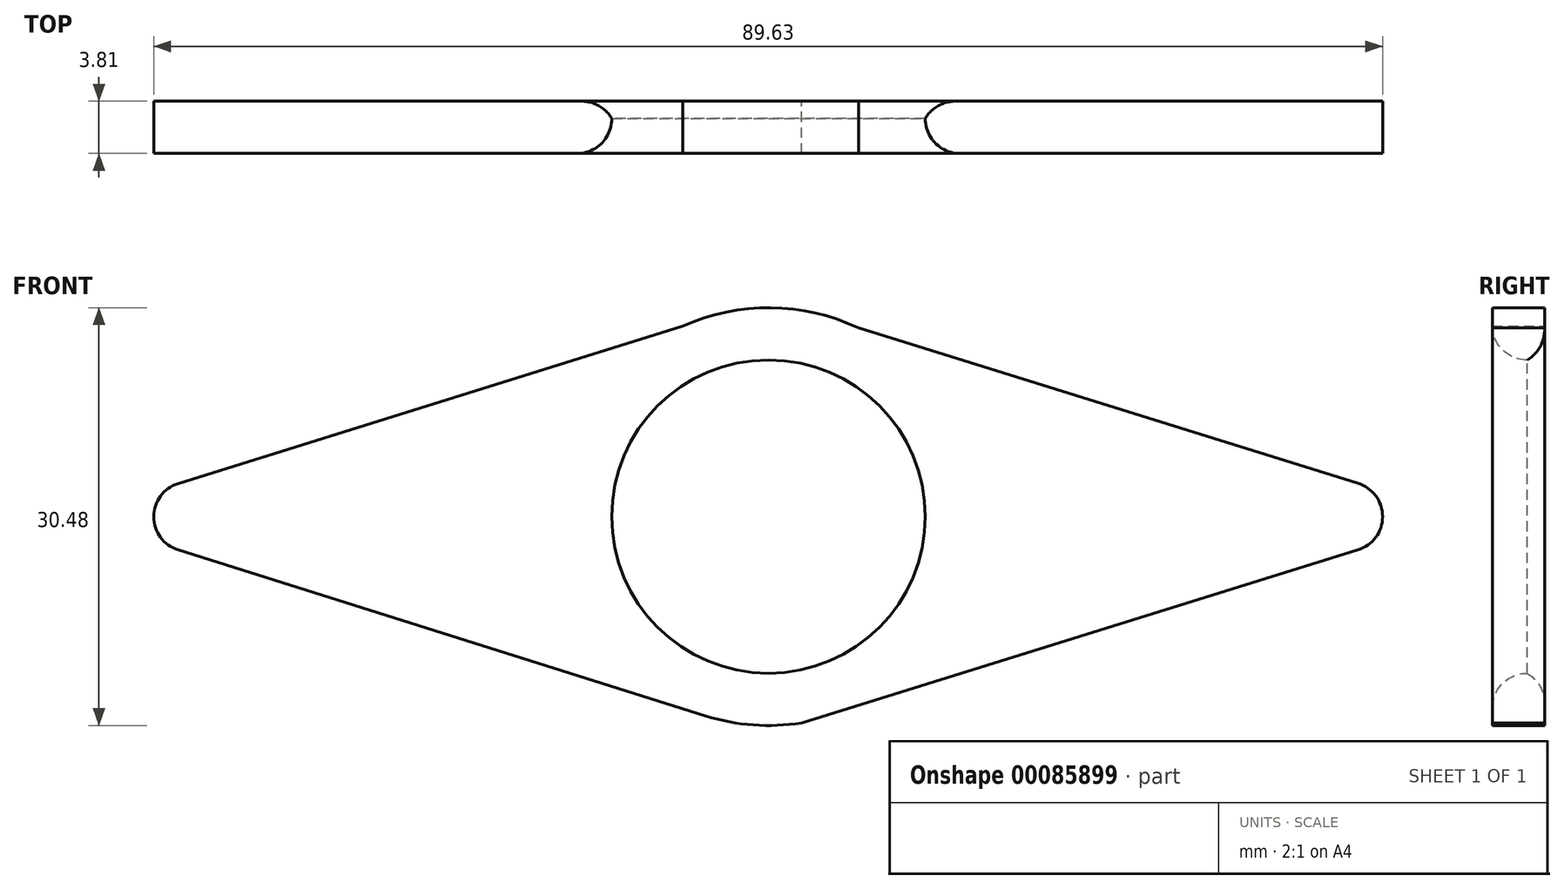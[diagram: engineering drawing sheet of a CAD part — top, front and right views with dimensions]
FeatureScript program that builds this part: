
annotation { "Feature Type Name" : "Feature", "Feature Type Description" : "" }
export const myFeature = defineFeature(function(context is Context, id is Id, definition is map)
    precondition{}
    {
        {
            var Q0;
            Q0=qCreatedBy(makeId("Front.planeOp"),FACE);
            var sketch = newSketch(context, id + "F0", { "sketchPlane" : qUnion([Q0])});
            skCircle(sketch, "E0", {"center": v(0, 0) * mm, "radius": 11.43 * mm});
            skArc(sketch, "E1", {"start": v(2.4, 15.05) * mm, "mid": v(-1.16, 15.2) * mm, "end": v(-4.66, 14.51) * mm});
            skLineSegment(sketch, "E2", {"start": v(2.4, 15.05) * mm, "end": v(50.8, 0) * mm});
            skLineSegment(sketch, "E3", {"start": v(50.8, 0) * mm, "end": v(2.4, -15.05) * mm});
            skArc(sketch, "E4.trimOffspring", {"start": v(6.56, 13.76) * mm, "mid": v(0.17, 15.24) * mm, "end": v(-6.25, 13.9) * mm});
            skArc(sketch, "E5", {"start": v(-6.24, -13.9) * mm, "mid": v(-2, -15.1) * mm, "end": v(2.4, -15.05) * mm});
            skLineSegment(sketch, "E6", {"start": v(-50.8, 0) * mm, "end": v(-2.94, -15.05) * mm});
            skLineSegment(sketch, "E7", {"start": v(-6.25, 13.9) * mm, "end": v(-50.8, 0) * mm});
            skArc(sketch, "E8.trimOffspring", {"start": v(2.4, 15.05) * mm, "mid": v(-2, 15.1) * mm, "end": v(-6.25, 13.9) * mm});
            skSolve(sketch);
        }
        {
            var Q0;
            Q0 = qSketchRegion(id + "F0", true);
            extrude(context, id + "F1", {"entities" : qUnion([Q0]), "depth" : 3.8 * mm});
        }
        {
            var Q0;
            Q0=makeQuery(id+"F1.opExtrude","SWEPT_EDGE",EDGE,{"disambiguationData":[OSD([sQuery(id+"F0.wireOp",EDGE,"E2"),sQuery(id+"F0.wireOp",EDGE,"E3")])]});
            var Q1;
            Q1=makeQuery(id+"F1.opExtrude","SWEPT_EDGE",EDGE,{"disambiguationData":[OSD([sQuery(id+"F0.wireOp",EDGE,"E6"),sQuery(id+"F0.wireOp",EDGE,"E7")])]});
            var Q2;
            Q2=makeQuery(id+"F1.opExtrude","CAP_EDGE",EDGE,{"disambiguationData":[OSD([sQuery(id+"F0.wireOp",EDGE,"E0")])],"isStart":false});
            fillet(context, id + "F2", {"entities" : qUnion([Q0, Q1, Q2]), "radius" : 2.54 * mm, "tangentPropagation" : true, "allowEdgeOverflow" : false});
        }
        {
            var Q0;
            Q0=makeQuery(id+"F1.opExtrude","CAP_EDGE",EDGE,{"disambiguationData":[OSD([sQuery(id+"F0.wireOp",EDGE,"E0")])],"isStart":true});
            fillet(context, id + "F3", {"entities" : qUnion([Q0]), "radius" : 2.54 * mm, "tangentPropagation" : true, "allowEdgeOverflow" : false});
        }
    });
